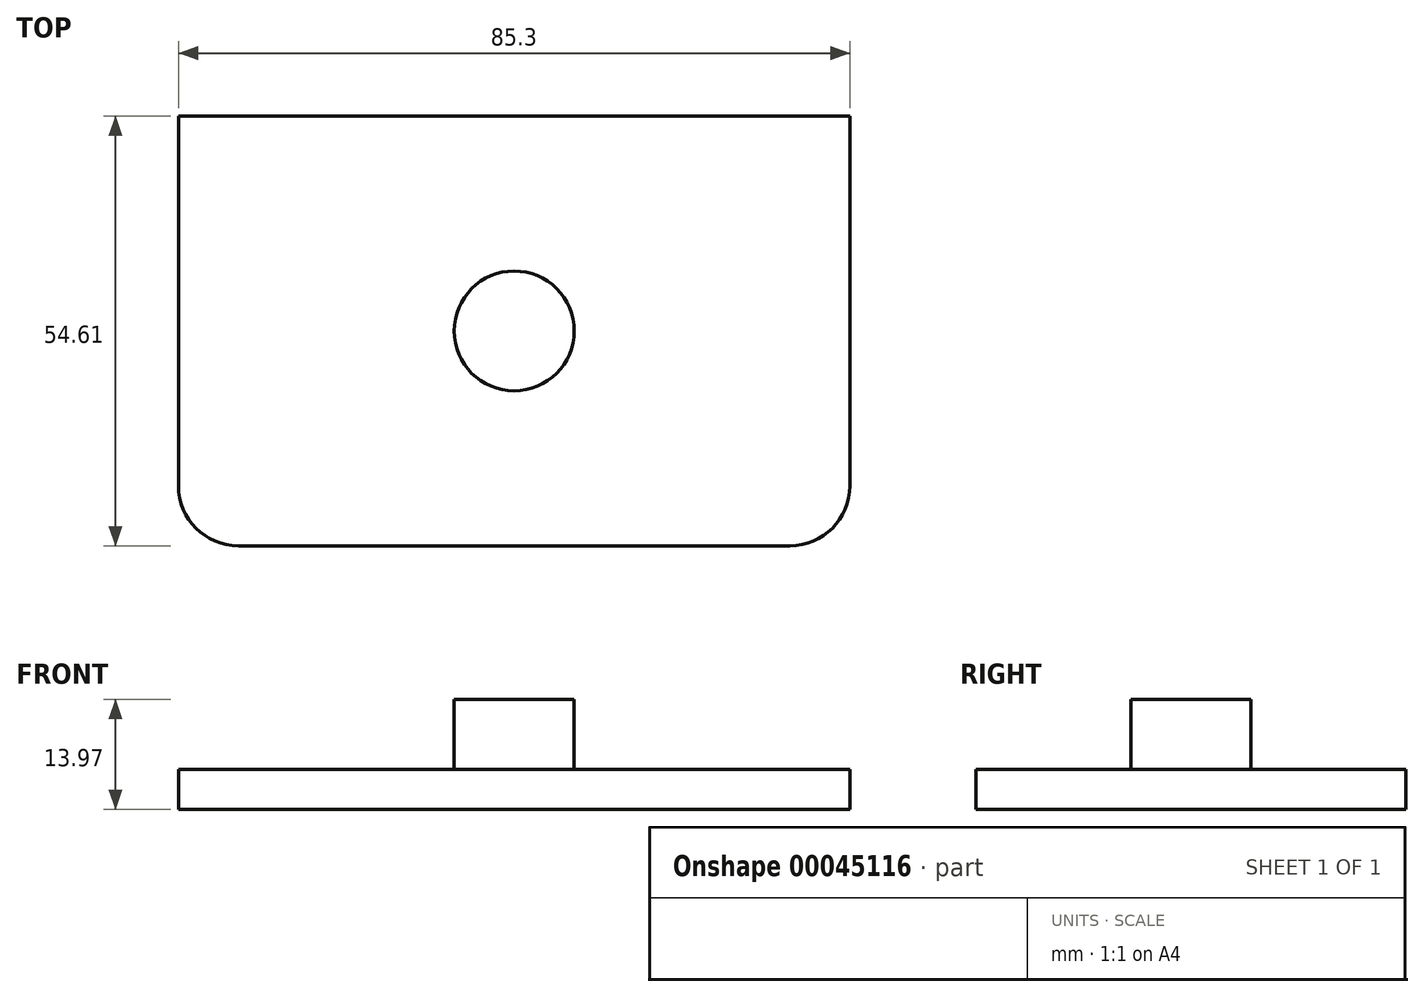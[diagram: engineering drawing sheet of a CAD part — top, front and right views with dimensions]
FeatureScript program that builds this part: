
annotation { "Feature Type Name" : "Feature", "Feature Type Description" : "" }
export const myFeature = defineFeature(function(context is Context, id is Id, definition is map)
    precondition{}
    {
        {
            var Q0;
            Q0=qCreatedBy(makeId("Top.planeOp"),FACE);
            var sketch = newSketch(context, id + "F0", { "sketchPlane" : qUnion([Q0])});
            skCircle(sketch, "E0", {"center": v(0, 0) * mm, "radius": 7.62 * mm});
            skLineSegment(sketch, "E1.rect.bottom", {"start": v(42.65, 27.3) * mm, "end": v(-42.65, 27.3) * mm});
            skLineSegment(sketch, "E1.rect.top", {"start": v(42.65, -27.3) * mm, "end": v(-42.65, -27.3) * mm});
            skLineSegment(sketch, "E1.rect.left", {"start": v(42.65, 27.3) * mm, "end": v(42.65, -27.3) * mm});
            skLineSegment(sketch, "E1.rect.right", {"start": v(-42.65, 27.3) * mm, "end": v(-42.65, -27.3) * mm});
            skSolve(sketch);
        }
        {
            var Q0;
            Q0=makeQuery(id+"F0.imprint","IMPRINT",FACE,{"disambiguationData":[TD([[makeQuery(id+"F0.imprint","IMPRINT",EDGE,{"derivedFrom":sQuery(id+"F0.wireOp",EDGE,"E0")}),1.0]])]});
            extrude(context, id + "F1", {"entities" : qUnion([Q0]), "depth" : 8.9 * mm});
        }
        {
            var Q0;
            Q0=makeQuery(id+"F0.imprint","IMPRINT",FACE,{"disambiguationData":[TD([[makeQuery(id+"F0.imprint","IMPRINT",EDGE,{"derivedFrom":sQuery(id+"F0.wireOp",EDGE,"E0")}),-1.0]])]});
            var Q1;
            Q1=makeQuery(id+"F0.imprint","IMPRINT",FACE,{"disambiguationData":[TD([[makeQuery(id+"F0.imprint","IMPRINT",EDGE,{"derivedFrom":sQuery(id+"F0.wireOp",EDGE,"E0")}),1.0]])]});
            extrude(context, id + "F2", {"entities" : qUnion([Q0, Q1]), "operationType" : NewBodyOperationType.ADD, "oppositeDirection" : true, "depth" : 5.08 * mm});
        }
        {
            var Q0;
            Q0=makeQuery(id+"F2.opExtrude","SWEPT_EDGE",EDGE,{"disambiguationData":[OSD([sQuery(id+"F0.wireOp",EDGE,"E1.rect.top"),sQuery(id+"F0.wireOp",EDGE,"E1.rect.left")])]});
            var Q1;
            Q1=makeQuery(id+"F2.opExtrude","SWEPT_EDGE",EDGE,{"disambiguationData":[OSD([sQuery(id+"F0.wireOp",EDGE,"E1.rect.top"),sQuery(id+"F0.wireOp",EDGE,"E1.rect.right")])]});
            fillet(context, id + "F3", {"entities" : qUnion([Q0, Q1]), "radius" : 7.62 * mm, "tangentPropagation" : true, "allowEdgeOverflow" : false});
        }
    });
